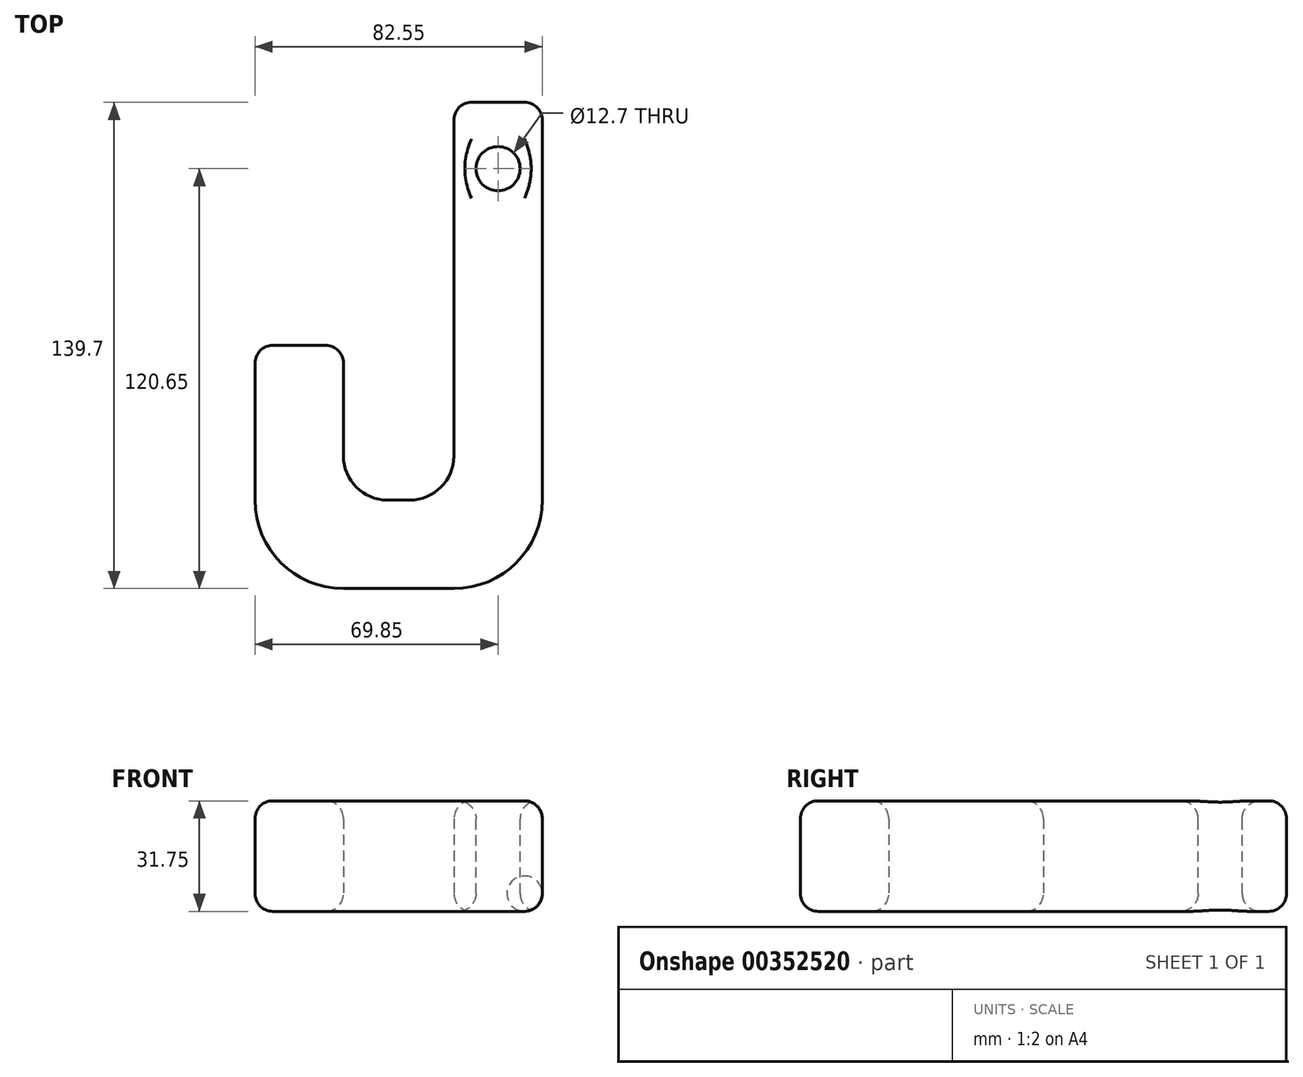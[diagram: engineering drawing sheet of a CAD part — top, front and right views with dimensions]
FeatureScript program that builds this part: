
annotation { "Feature Type Name" : "Feature", "Feature Type Description" : "" }
export const myFeature = defineFeature(function(context is Context, id is Id, definition is map)
    precondition{}
    {
        {
            var Q0;
            Q0=qCreatedBy(makeId("Top.planeOp"),FACE);
            var sketch = newSketch(context, id + "F0", { "sketchPlane" : qUnion([Q0])});
            skLineSegment(sketch, "E0", {"start": v(0, 0) * mm, "end": v(0, 69.85) * mm});
            skLineSegment(sketch, "E1", {"start": v(0, 69.85) * mm, "end": v(25.4, 69.85) * mm});
            skLineSegment(sketch, "E2", {"start": v(25.4, 69.85) * mm, "end": v(25.4, 25.4) * mm});
            skLineSegment(sketch, "E3", {"start": v(25.4, 25.4) * mm, "end": v(57.15, 25.4) * mm});
            skLineSegment(sketch, "E4", {"start": v(57.15, 25.4) * mm, "end": v(57.15, 139.7) * mm});
            skLineSegment(sketch, "E5", {"start": v(57.15, 139.7) * mm, "end": v(82.55, 139.7) * mm});
            skLineSegment(sketch, "E6", {"start": v(82.55, 139.7) * mm, "end": v(82.55, 0) * mm});
            skLineSegment(sketch, "E7", {"start": v(82.55, 0) * mm, "end": v(0, 0) * mm});
            skSolve(sketch);
        }
        {
            var Q0;
            Q0 = qSketchRegion(id + "F0", true);
            extrude(context, id + "F1", {"entities" : qUnion([Q0]), "depth" : 31.75 * mm});
        }
        {
            var Q0;
            Q0=makeQuery(id+"F1.opExtrude","CAP_FACE",FACE,{"disambiguationData":[OSD([sQuery(id+"F0.wireOp",EDGE,"E0"),sQuery(id+"F0.wireOp",EDGE,"E1"),sQuery(id+"F0.wireOp",EDGE,"E2"),sQuery(id+"F0.wireOp",EDGE,"E3"),sQuery(id+"F0.wireOp",EDGE,"E4"),sQuery(id+"F0.wireOp",EDGE,"E5"),sQuery(id+"F0.wireOp",EDGE,"E6"),sQuery(id+"F0.wireOp",EDGE,"E7")])],"isStart":false});
            var sketch = newSketch(context, id + "F2", { "sketchPlane" : qUnion([Q0])});
            skCircle(sketch, "E8", {"center": v(69.85, 120.65) * mm, "radius": 6.35 * mm});
            skLineSegment(sketch, "E9", {"start": v(69.85, 139.7) * mm, "end": v(69.85, 86.62) * mm, "construction": true});
            skSolve(sketch);
        }
        {
            var Q0;
            Q0 = qSketchRegion(id + "F2", true);
            var Q1;
            Q1=makeQuery(id+"F1.opExtrude","CAP_FACE",FACE,{"disambiguationData":[OSD([sQuery(id+"F0.wireOp",EDGE,"E0"),sQuery(id+"F0.wireOp",EDGE,"E1"),sQuery(id+"F0.wireOp",EDGE,"E2"),sQuery(id+"F0.wireOp",EDGE,"E3"),sQuery(id+"F0.wireOp",EDGE,"E4"),sQuery(id+"F0.wireOp",EDGE,"E5"),sQuery(id+"F0.wireOp",EDGE,"E6"),sQuery(id+"F0.wireOp",EDGE,"E7")])],"isStart":true});
            extrude(context, id + "F3", {"entities" : qUnion([Q0]), "operationType" : NewBodyOperationType.REMOVE, "endBound" : BoundingType.UP_TO_SURFACE, "oppositeDirection" : true, "endBoundEntityFace" : qUnion([Q1]), "depth" : 25.4 * mm});
        }
        {
            var Q0;
            Q0=makeQuery(id+"F1.opExtrude","SWEPT_EDGE",EDGE,{"disambiguationData":[OSD([sQuery(id+"F0.wireOp",EDGE,"E2"),sQuery(id+"F0.wireOp",EDGE,"E3")])]});
            var Q1;
            Q1=makeQuery(id+"F1.opExtrude","SWEPT_EDGE",EDGE,{"disambiguationData":[OSD([sQuery(id+"F0.wireOp",EDGE,"E3"),sQuery(id+"F0.wireOp",EDGE,"E4")])]});
            fillet(context, id + "F4", {"entities" : qUnion([Q0, Q1]), "radius" : 12.7 * mm, "tangentPropagation" : true, "allowEdgeOverflow" : false});
        }
        {
            var Q0;
            Q0=makeQuery(id+"F1.opExtrude","SWEPT_EDGE",EDGE,{"disambiguationData":[OSD([sQuery(id+"F0.wireOp",EDGE,"E0"),sQuery(id+"F0.wireOp",EDGE,"E7")])]});
            var Q1;
            Q1=makeQuery(id+"F1.opExtrude","SWEPT_EDGE",EDGE,{"disambiguationData":[OSD([sQuery(id+"F0.wireOp",EDGE,"E6"),sQuery(id+"F0.wireOp",EDGE,"E7")])]});
            fillet(context, id + "F5", {"entities" : qUnion([Q0, Q1]), "radius" : 25.4 * mm, "tangentPropagation" : true, "allowEdgeOverflow" : false});
        }
        {
            var Q0;
            Q0=makeQuery(id+"F1.opExtrude","SWEPT_EDGE",EDGE,{"disambiguationData":[OSD([sQuery(id+"F0.wireOp",EDGE,"E1"),sQuery(id+"F0.wireOp",EDGE,"E2")])]});
            var Q1;
            Q1=makeQuery(id+"F1.opExtrude","SWEPT_EDGE",EDGE,{"disambiguationData":[OSD([sQuery(id+"F0.wireOp",EDGE,"E0"),sQuery(id+"F0.wireOp",EDGE,"E1")])]});
            var Q2;
            Q2=makeQuery(id+"F1.opExtrude","SWEPT_EDGE",EDGE,{"disambiguationData":[OSD([sQuery(id+"F0.wireOp",EDGE,"E5"),sQuery(id+"F0.wireOp",EDGE,"E6")])]});
            var Q3;
            Q3=makeQuery(id+"F1.opExtrude","CAP_EDGE",EDGE,{"disambiguationData":[OSD([sQuery(id+"F0.wireOp",EDGE,"E5")])],"isStart":false});
            var Q4;
            Q4=makeQuery(id+"F1.opExtrude","SWEPT_EDGE",EDGE,{"disambiguationData":[OSD([sQuery(id+"F0.wireOp",EDGE,"E4"),sQuery(id+"F0.wireOp",EDGE,"E5")])]});
            var Q5;
            Q5=makeQuery(id+"F1.opExtrude","CAP_EDGE",EDGE,{"disambiguationData":[OSD([sQuery(id+"F0.wireOp",EDGE,"E5")])],"isStart":true});
            fillet(context, id + "F6", {"entities" : qUnion([Q0, Q1, Q2, Q3, Q4, Q5]), "radius" : 5.08 * mm, "tangentPropagation" : true, "allowEdgeOverflow" : false});
        }
        {
            var Q0;
            Q0=makeQuery(id+"F1.opExtrude","CAP_EDGE",EDGE,{"disambiguationData":[OSD([sQuery(id+"F0.wireOp",EDGE,"E4")])],"isStart":false});
            var Q1;
            Q1=makeQuery(id+"F1.opExtrude","CAP_FACE",FACE,{"disambiguationData":[OSD([sQuery(id+"F0.wireOp",EDGE,"E0"),sQuery(id+"F0.wireOp",EDGE,"E1"),sQuery(id+"F0.wireOp",EDGE,"E2"),sQuery(id+"F0.wireOp",EDGE,"E3"),sQuery(id+"F0.wireOp",EDGE,"E4"),sQuery(id+"F0.wireOp",EDGE,"E5"),sQuery(id+"F0.wireOp",EDGE,"E6"),sQuery(id+"F0.wireOp",EDGE,"E7")])],"isStart":true});
            var Q2;
            Q2=makeQuery(id+"F3.boolean.opBoolean","COPY",FACE,{"derivedFrom":makeQuery(id+"F3.opExtrude","SWEPT_FACE",FACE,{"disambiguationData":[OSD([sQuery(id+"F2.wireOp",EDGE,"E8")])]})});
            fillet(context, id + "F7", {"entities" : qUnion([Q0, Q1, Q2]), "radius" : 5.08 * mm, "tangentPropagation" : true, "allowEdgeOverflow" : false});
        }
    });
